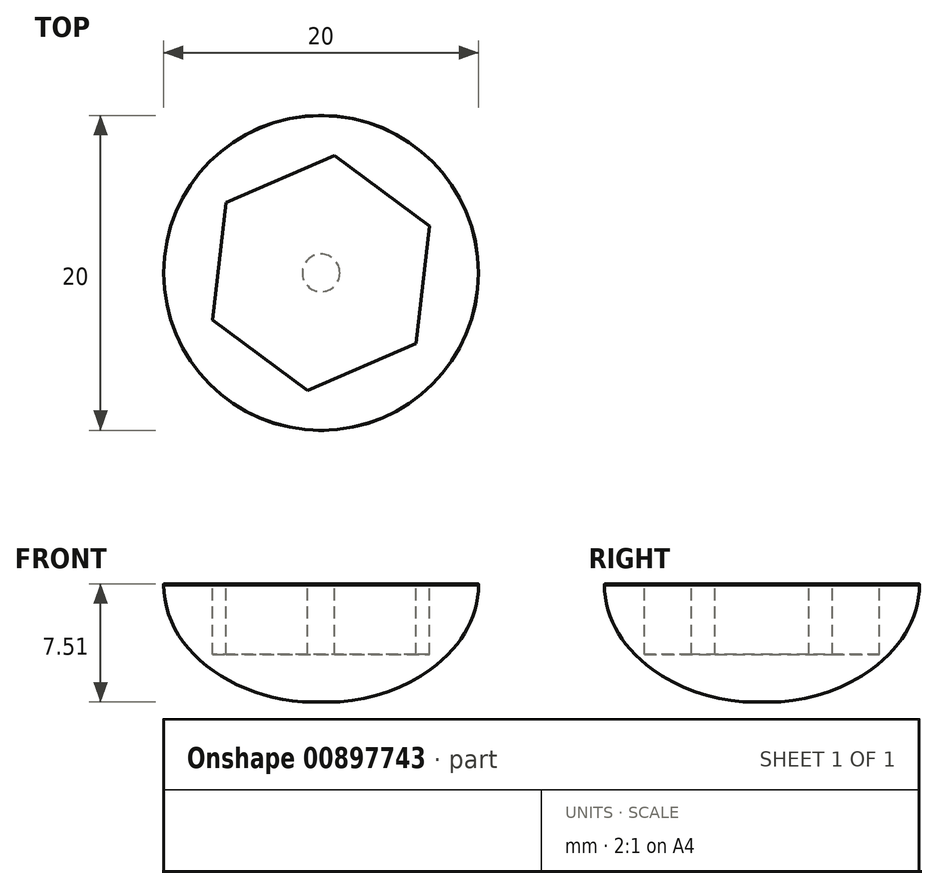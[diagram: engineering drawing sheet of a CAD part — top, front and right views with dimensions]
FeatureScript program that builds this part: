
annotation { "Feature Type Name" : "Feature", "Feature Type Description" : "" }
export const myFeature = defineFeature(function(context is Context, id is Id, definition is map)
    precondition{}
    {
        {
            var Q0;
            Q0=qCreatedBy(makeId("Front.planeOp"),FACE);
            var sketch = newSketch(context, id + "F0", { "sketchPlane" : qUnion([Q0])});
            skLineSegment(sketch, "E0", {"start": v(0, 0.05) * mm, "end": v(0, 30) * mm});
            skEllipticalArc(sketch, "E1", {});
            skFitSpline(sketch, "E2", {"points": [v(-10, 7.5) * mm, v(-6.69, 11.5) * mm, v(-5.1, 14.95) * mm, v(-4.1, 20.28) * mm, v(-2.44, 27.2) * mm, v(0, 30) * mm], "startDerivative": vector(2.9, 37.54) * mm, "endDerivative": vector(24.45, -0.45) * mm});
            skPoint(sketch, "E3.orphan", {"position": v(10, 7.5) * mm});
            skLineSegment(sketch, "E4", {"start": v(-1.2, 0.05) * mm, "end": v(0, 0.05) * mm});
            skPoint(sketch, "E5.orphan", {"position": v(0, 0) * mm});
            const initialGuessF0  = {"E1": [0, 0.0075, 1, 0, 0.01, 0.0075, 3.141592653589793, 4.592936546162219]};
            skSetInitialGuess(sketch, initialGuessF0);
            skSolve(sketch);
        }
        {
            var Q0;
            Q0=makeQuery(id+"F0.imprint","IMPRINT",FACE,{"disambiguationData":[TD([[makeQuery(id+"F0.imprint","IMPRINT",EDGE,{"derivedFrom":sQuery(id+"F0.wireOp",EDGE,"E0")}),1.0]])]});
            var Q1;
            Q1=sQuery(id+"F0.wireOp",EDGE,"E0");
            revolve(context, id + "F1", {"surfaceOperationType" : NewSurfaceOperationType.NEW, "entities" : qUnion([Q0]), "axis" : qUnion([Q1]), "revolveType" : RevolveType.FULL});
        }
        {
            var Q0;
            Q0=qCreatedBy(makeId("Front.planeOp"),FACE);
            var sketch = newSketch(context, id + "F2", { "sketchPlane" : qUnion([Q0])});
            skLineSegment(sketch, "E6.bottom", {"start": v(0, 7.56) * mm, "end": v(23.88, 7.56) * mm});
            skLineSegment(sketch, "E6.top", {"start": v(0, 34.3) * mm, "end": v(23.88, 34.3) * mm});
            skLineSegment(sketch, "E6.left", {"start": v(0, 7.56) * mm, "end": v(0, 34.3) * mm});
            skLineSegment(sketch, "E6.right", {"start": v(23.88, 7.56) * mm, "end": v(23.88, 34.3) * mm});
            skSolve(sketch);
        }
        {
            var Q0;
            Q0=makeQuery(id+"F2.imprint","IMPRINT",FACE,{"disambiguationData":[TD([[makeQuery(id+"F2.imprint","IMPRINT",EDGE,{"derivedFrom":sQuery(id+"F2.wireOp",EDGE,"E6.bottom")}),1.0]])]});
            var Q1;
            Q1=sQuery(id+"F2.wireOp",EDGE,"E6.left");
            revolve(context, id + "F3", {"operationType" : NewBodyOperationType.REMOVE, "surfaceOperationType" : NewSurfaceOperationType.NEW, "entities" : qUnion([Q0]), "axis" : qUnion([Q1]), "revolveType" : RevolveType.FULL, "oppositeDirection" : true});
        }
        {
            var Q0;
            Q0=makeQuery(id+"F3.boolean.opBoolean","COPY",FACE,{"derivedFrom":makeQuery(id+"F3.opRevolve","SWEPT_FACE",FACE,{"disambiguationData":[OSD([sQuery(id+"F2.wireOp",EDGE,"E6.bottom")])]})});
            var sketch = newSketch(context, id + "F4", { "sketchPlane" : qUnion([Q0])});
            skCircle(sketch, "E7.cCircle", {"center": v(0, 0) * mm, "radius": 6.5 * mm, "construction": true});
            skLineSegment(sketch, "E7.0", {"start": v(6.02, -4.48) * mm, "end": v(-0.86, -7.46) * mm});
            skLineSegment(sketch, "E7.1", {"start": v(-0.86, -7.46) * mm, "end": v(-6.89, -2.98) * mm});
            skLineSegment(sketch, "E7.2", {"start": v(-6.89, -2.98) * mm, "end": v(-6.02, 4.48) * mm});
            skLineSegment(sketch, "E7.3", {"start": v(-6.02, 4.48) * mm, "end": v(0.86, 7.46) * mm});
            skLineSegment(sketch, "E7.4", {"start": v(0.86, 7.46) * mm, "end": v(6.89, 2.98) * mm});
            skLineSegment(sketch, "E7.5", {"start": v(6.89, 2.98) * mm, "end": v(6.02, -4.48) * mm});
            skPoint(sketch, "E7.0.midPoint", {"position": v(2.58, -5.97) * mm});
            skSolve(sketch);
        }
        {
            var Q0;
            Q0=makeQuery(id+"F4.imprint","IMPRINT",FACE,{"disambiguationData":[TD([[makeQuery(id+"F4.imprint","IMPRINT",EDGE,{"derivedFrom":sQuery(id+"F4.wireOp",EDGE,"E7.0")}),-1.0]])]});
            extrude(context, id + "F5", {"entities" : qUnion([Q0]), "operationType" : NewBodyOperationType.REMOVE, "oppositeDirection" : true, "depth" : 4.5 * mm, "offsetDistance" : 25 * mm});
        }
    });
